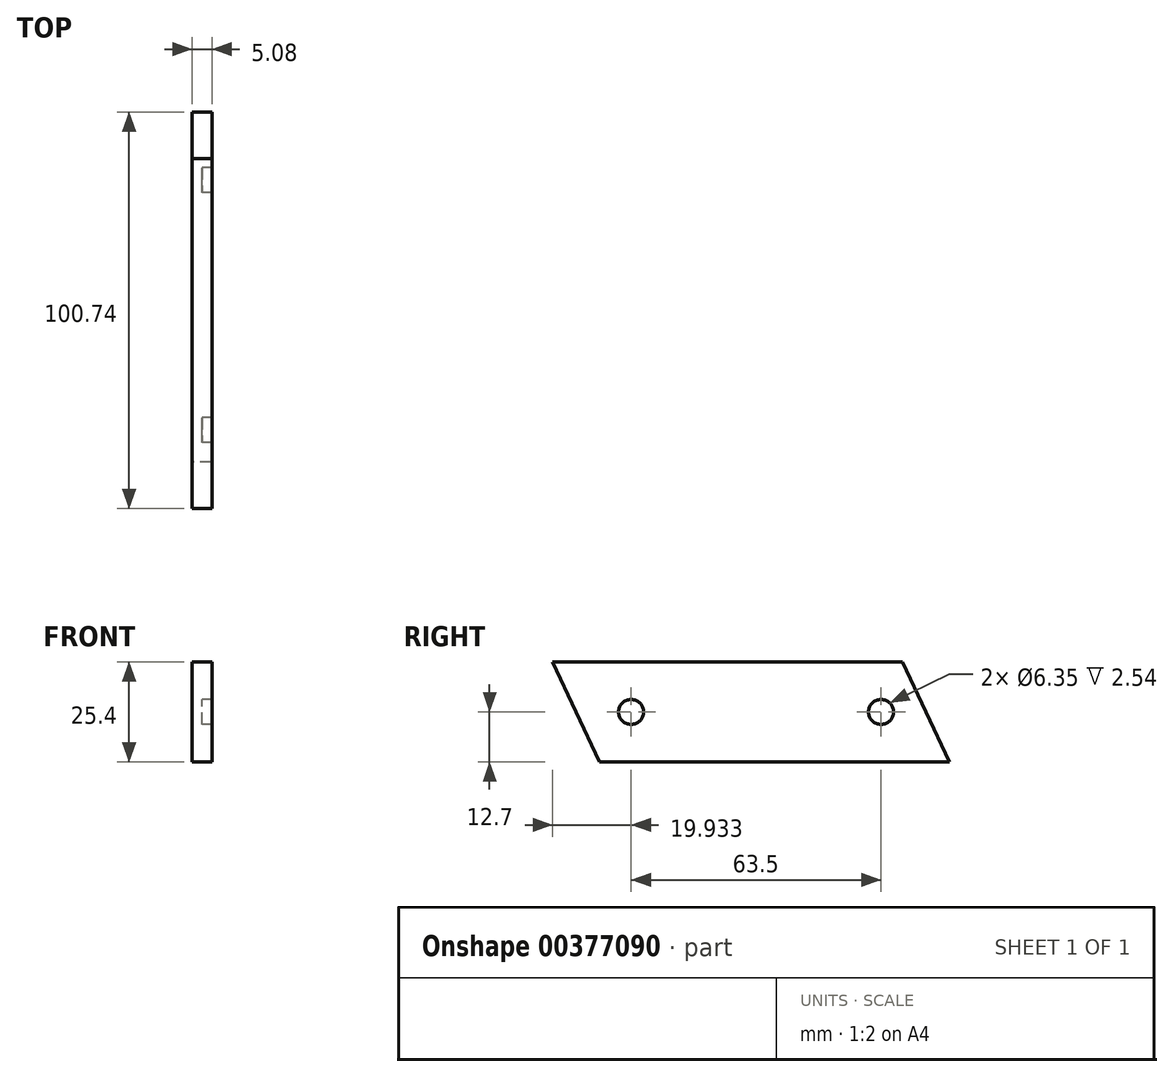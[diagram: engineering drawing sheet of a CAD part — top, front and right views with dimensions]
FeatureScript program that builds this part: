
annotation { "Feature Type Name" : "Feature", "Feature Type Description" : "" }
export const myFeature = defineFeature(function(context is Context, id is Id, definition is map)
    precondition{}
    {
        {
            var Q0;
            Q0=qCreatedBy(makeId("Right.planeOp"),FACE);
            var sketch = newSketch(context, id + "F0", { "sketchPlane" : qUnion([Q0])});
            skLineSegment(sketch, "E0.bottom", {"start": v(38.53, 12.7) * mm, "end": v(-50.37, 12.7) * mm});
            skLineSegment(sketch, "E0.top", {"start": v(50.37, -12.7) * mm, "end": v(-38.53, -12.7) * mm});
            skLineSegment(sketch, "E0.left", {"start": v(38.53, 12.7) * mm, "end": v(50.37, -12.7) * mm});
            skLineSegment(sketch, "E0.right", {"start": v(-50.37, 12.7) * mm, "end": v(-38.53, -12.7) * mm});
            skPoint(sketch, "E0.middle", {"position": v(0, 0) * mm});
            skLineSegment(sketch, "E1", {"start": v(-38.53, -12.7) * mm, "end": v(-38.53, 12.7) * mm, "construction": true});
            skCircle(sketch, "E2", {"center": v(-30.44, 0) * mm, "radius": 3.18 * mm});
            skCircle(sketch, "E3", {"center": v(33.06, 0) * mm, "radius": 3.18 * mm});
            skSolve(sketch);
        }
        {
            var Q0;
            Q0 = qSketchRegion(id + "F0", true);
            extrude(context, id + "F1", {"entities" : qUnion([Q0]), "depth" : 2.54 * mm});
        }
        {
            var Q0;
            Q0=makeQuery(id+"F1.opExtrude","CAP_FACE",FACE,{"disambiguationData":[OSD([sQuery(id+"F0.wireOp",EDGE,"E0.bottom"),sQuery(id+"F0.wireOp",EDGE,"E0.top"),sQuery(id+"F0.wireOp",EDGE,"E0.left"),sQuery(id+"F0.wireOp",EDGE,"E0.right"),sQuery(id+"F0.wireOp",EDGE,"E2"),sQuery(id+"F0.wireOp",EDGE,"E3")])],"isStart":true});
            var sketch = newSketch(context, id + "F2", { "sketchPlane" : qUnion([Q0])});
            skSolve(sketch);
        }
        {
            var Q0;
            Q0 = qSketchRegion(id + "F2", true);
            var Q1;
            Q1=makeQuery(id+"F2.imprint","IMPRINT",FACE,{"disambiguationData":[TD([[makeQuery(id+"F2.imprint","IMPRINT",EDGE,{"derivedFrom":makeQuery(id+"F1.opExtrude","CAP_EDGE",EDGE,{"disambiguationData":[OSD([sQuery(id+"F0.wireOp",EDGE,"E0.bottom")])],"isStart":true})}),-1.0]])]});
            var Q2;
            Q2=makeQuery(id+"F2.imprint","IMPRINT",FACE,{"disambiguationData":[TD([[makeQuery(id+"F2.imprint","IMPRINT",EDGE,{"derivedFrom":makeQuery(id+"F1.opExtrude","CAP_EDGE",EDGE,{"disambiguationData":[OSD([sQuery(id+"F0.wireOp",EDGE,"E3")])],"isStart":true})}),-1.0]])]});
            var Q3;
            Q3=makeQuery(id+"F2.imprint","IMPRINT",FACE,{"disambiguationData":[TD([[makeQuery(id+"F2.imprint","IMPRINT",EDGE,{"derivedFrom":makeQuery(id+"F1.opExtrude","CAP_EDGE",EDGE,{"disambiguationData":[OSD([sQuery(id+"F0.wireOp",EDGE,"E2")])],"isStart":true})}),-1.0]])]});
            extrude(context, id + "F3", {"entities" : qUnion([Q0, Q1, Q2, Q3]), "operationType" : NewBodyOperationType.ADD, "depth" : 2.54 * mm});
        }
    });
